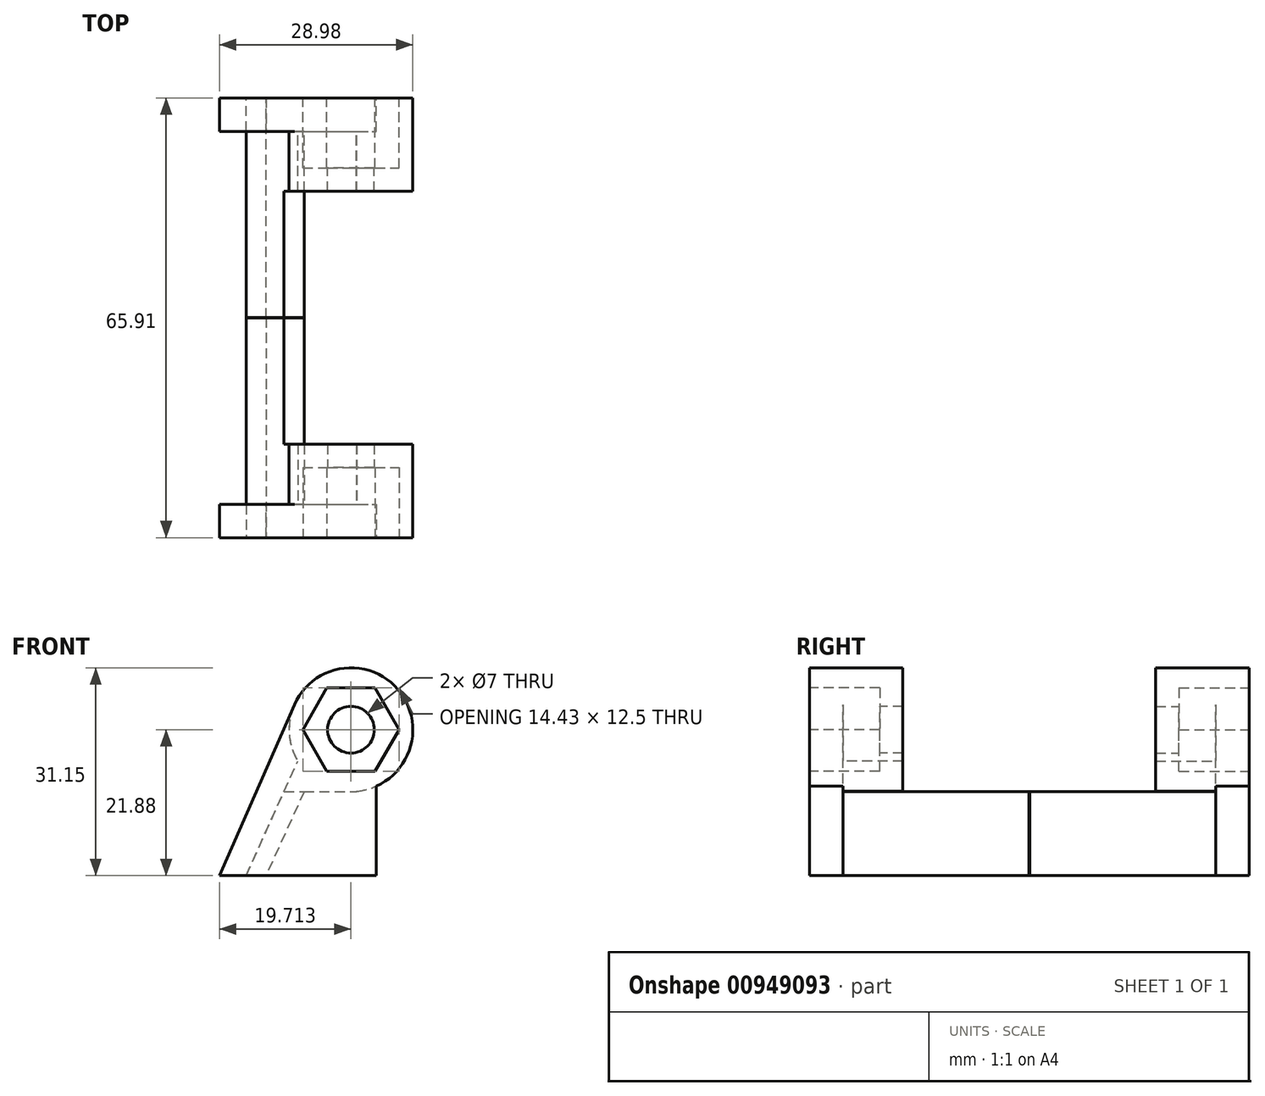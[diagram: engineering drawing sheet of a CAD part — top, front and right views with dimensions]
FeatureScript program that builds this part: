
annotation { "Feature Type Name" : "Feature", "Feature Type Description" : "" }
export const myFeature = defineFeature(function(context is Context, id is Id, definition is map)
    precondition{}
    {
        {
            var Q0;
            Q0=qCreatedBy(makeId("Front.planeOp"),FACE);
            var sketch = newSketch(context, id + "F0", { "sketchPlane" : qUnion([Q0])});
            skLineSegment(sketch, "E0", {"start": v(-38, 25.4) * mm, "end": v(-49, 3.56) * mm});
            skLineSegment(sketch, "E1", {"start": v(-49, 3.56) * mm, "end": v(-25.5, 3.56) * mm});
            skLineSegment(sketch, "E2", {"start": v(-25.5, 3.56) * mm, "end": v(-25.5, 19.16) * mm});
            skLineSegment(sketch, "E3", {"start": v(-25.5, 19.16) * mm, "end": v(-37, 19.16) * mm});
            skLineSegment(sketch, "E4", {"start": v(-37, 19.16) * mm, "end": v(-37, 25.4) * mm});
            skCircle(sketch, "E5", {"center": v(-29.29, 25.4) * mm, "radius": 9.27 * mm});
            skCircle(sketch, "E6.cCircle", {"center": v(-29.29, 25.4) * mm, "radius": 6.25 * mm, "construction": true});
            skLineSegment(sketch, "E6.0", {"start": v(-25.68, 31.66) * mm, "end": v(-22.07, 25.4) * mm});
            skLineSegment(sketch, "E6.1", {"start": v(-22.07, 25.4) * mm, "end": v(-25.68, 19.16) * mm});
            skLineSegment(sketch, "E6.2", {"start": v(-25.68, 19.16) * mm, "end": v(-32.9, 19.16) * mm});
            skLineSegment(sketch, "E6.3", {"start": v(-32.9, 19.16) * mm, "end": v(-36.5, 25.4) * mm});
            skLineSegment(sketch, "E6.4", {"start": v(-36.5, 25.4) * mm, "end": v(-32.9, 31.66) * mm});
            skLineSegment(sketch, "E6.5", {"start": v(-32.9, 31.66) * mm, "end": v(-25.68, 31.66) * mm});
            skCircle(sketch, "E7", {"center": v(-29.29, 25.4) * mm, "radius": 3.5 * mm});
            skPoint(sketch, "E8", {"position": v(-37, 3.56) * mm});
            skLineSegment(sketch, "E9", {"start": v(-37, 19.16) * mm, "end": v(-37, 3.56) * mm});
            skLineSegment(sketch, "E10", {"start": v(-38, 25.4) * mm, "end": v(-37, 25.4) * mm});
            skLineSegment(sketch, "E11", {"start": v(-49, 3.56) * mm, "end": v(-36.67, 31.66) * mm});
            skSolve(sketch);
        }
        {
            var Q0;
            {var subQ0=sQuery(id+"F0.wireOp",EDGE,"E11");var subQ3=sQuery(id+"F0.wireOp",EDGE,"E5");var subQ5=makeQuery(id+"F0.imprint","INTERSECT",VERTEX,{"derivedFrom":[subQ3,subQ0]});Q0=makeQuery(id+"F0.imprint","IMPRINT",FACE,{"disambiguationData":[TD([[makeQuery(id+"F0.imprint","IMPRINT",EDGE,{"disambiguationData":[TD([[subQ5,-1.0]])],"derivedFrom":subQ3}),-1.0]])]});}
            var Q1;
            {var subQ0=sQuery(id+"F0.wireOp",EDGE,"E9");Q1=makeQuery(id+"F0.imprint","IMPRINT",FACE,{"disambiguationData":[TD([[makeQuery(id+"F0.imprint","IMPRINT",EDGE,{"derivedFrom":subQ0}),-1.0]])]});}
            var Q2;
            {var subQ0=sQuery(id+"F0.wireOp",EDGE,"E9");Q2=makeQuery(id+"F0.imprint","IMPRINT",FACE,{"disambiguationData":[TD([[makeQuery(id+"F0.imprint","IMPRINT",EDGE,{"derivedFrom":subQ0}),1.0]])]});}
            var Q3;
            {var subQ1=sQuery(id+"F0.wireOp",EDGE,"E3");var subQ3=sQuery(id+"F0.wireOp",EDGE,"E5");var subQ4=makeQuery(id+"F0.imprint","INTERSECT",VERTEX,{"derivedFrom":[subQ1,subQ3]});Q3=makeQuery(id+"F0.imprint","IMPRINT",FACE,{"disambiguationData":[TD([[makeQuery(id+"F0.imprint","IMPRINT",EDGE,{"disambiguationData":[TD([[subQ4,1.0]])],"derivedFrom":subQ3}),-1.0]])]});}
            extrude(context, id + "F1", {"entities" : qUnion([Q0, Q1, Q2, Q3]), "oppositeDirection" : true, "depth" : 5 * mm, "offsetDistance" : 25.4 * mm});
        }
        {
            var Q0;
            Q0=makeQuery(id+"F0.imprint","IMPRINT",FACE,{"disambiguationData":[TD([[makeQuery(id+"F0.imprint","IMPRINT",EDGE,{"derivedFrom":sQuery(id+"F0.wireOp",EDGE,"E6.0")}),1.0]])]});
            var Q1;
            {var subQ0=sQuery(id+"F0.wireOp",EDGE,"E3");var subQ1=sQuery(id+"F0.wireOp",EDGE,"E2");var subQ2=makeQuery(id+"F0.imprint","INTERSECT",VERTEX,{"derivedFrom":[subQ1,subQ0]});Q1=makeQuery(id+"F0.imprint","IMPRINT",FACE,{"disambiguationData":[TD([[makeQuery(id+"F0.imprint","IMPRINT",EDGE,{"disambiguationData":[TD([[subQ2,1.0]])],"derivedFrom":subQ1}),1.0]])]});}
            var Q2;
            {var subQ0=sQuery(id+"F0.wireOp",EDGE,"E10");Q2=makeQuery(id+"F0.imprint","IMPRINT",FACE,{"disambiguationData":[TD([[makeQuery(id+"F0.imprint","IMPRINT",EDGE,{"derivedFrom":subQ0}),-1.0]])]});}
            var Q3;
            Q3=makeQuery(id+"F0.imprint","IMPRINT",FACE,{"disambiguationData":[TD([[makeQuery(id+"F0.imprint","IMPRINT",EDGE,{"derivedFrom":sQuery(id+"F0.wireOp",EDGE,"E6.0")}),-1.0]])]});
            var Q4;
            Q4 = qSketchRegion(id + "F4", true);
            extrude(context, id + "F2", {"entities" : qUnion([Q0, Q1, Q2, Q3, Q4]), "operationType" : NewBodyOperationType.ADD, "oppositeDirection" : true, "depth" : 14 * mm, "offsetDistance" : 25.4 * mm});
        }
        {
            var Q0;
            Q0=makeQuery(id+"F0.imprint","IMPRINT",FACE,{"disambiguationData":[TD([[makeQuery(id+"F0.imprint","IMPRINT",EDGE,{"derivedFrom":sQuery(id+"F0.wireOp",EDGE,"E6.0")}),-1.0]])]});
            extrude(context, id + "F3", {"entities" : qUnion([Q0]), "operationType" : NewBodyOperationType.REMOVE, "oppositeDirection" : true, "depth" : 10.52 * mm, "offsetDistance" : 25.4 * mm});
        }
        {
            var Q0;
            Q0=qCreatedBy(makeId("Front.planeOp"),FACE);
            var sketch = newSketch(context, id + "F4", { "sketchPlane" : qUnion([Q0])});
            skLineSegment(sketch, "E12", {"start": v(-45, 3.53) * mm, "end": v(-39.32, 16.14) * mm});
            skLineSegment(sketch, "E13", {"start": v(-39.32, 16.14) * mm, "end": v(-36.32, 16.14) * mm});
            skLineSegment(sketch, "E14", {"start": v(-36.32, 16.14) * mm, "end": v(-42, 3.53) * mm});
            skLineSegment(sketch, "E15", {"start": v(-42, 3.53) * mm, "end": v(-45, 3.53) * mm});
            skLineSegment(sketch, "E16", {"start": v(-39.32, 16.14) * mm, "end": v(-28.4, 16.14) * mm});
            skLineSegment(sketch, "E17", {"start": v(-45, 3.53) * mm, "end": v(-36.96, 21.36) * mm});
            skLineSegment(sketch, "E18", {"start": v(-36.96, 21.36) * mm, "end": v(-28.4, 16.14) * mm});
            skSolve(sketch);
        }
        {
            var Q0;
            {var subQ0=sQuery(id+"F4.wireOp",EDGE,"E14");Q0=makeQuery(id+"F4.imprint","IMPRINT",FACE,{"disambiguationData":[TD([[makeQuery(id+"F4.imprint","IMPRINT",EDGE,{"derivedFrom":subQ0}),-1.0]])]});}
            extrude(context, id + "F5", {"entities" : qUnion([Q0]), "operationType" : NewBodyOperationType.ADD, "oppositeDirection" : true, "depth" : 33 * mm, "offsetDistance" : 25.4 * mm});
        }
        {
            var Q0;
            {var subQ4=sQuery(id+"F4.wireOp",EDGE,"E18");Q0=makeQuery(id+"F4.imprint","IMPRINT",FACE,{"disambiguationData":[TD([[makeQuery(id+"F4.imprint","IMPRINT",EDGE,{"derivedFrom":subQ4}),-1.0]])]});}
            extrude(context, id + "F6", {"entities" : qUnion([Q0]), "operationType" : NewBodyOperationType.ADD, "oppositeDirection" : true, "depth" : 14 * mm, "offsetDistance" : 25.4 * mm});
        }
        {
            var Q0;
            Q0=makeQuery(id+"F1.opExtrude","SWEPT_BODY",BODY,{"disambiguationData":[OSD([sQuery(id+"F0.wireOp",EDGE,"E1"),sQuery(id+"F0.wireOp",EDGE,"E2"),sQuery(id+"F0.wireOp",EDGE,"E5"),sQuery(id+"F0.wireOp",EDGE,"E11")])]});
            var Q1;
            Q1=qCreatedBy(makeId("Front.planeOp"),FACE);
            mirror(context, id + "F7", {"entities" : qUnion([Q0]), "mirrorPlane" : qUnion([Q1])});
        }
        {
            var Q0;
            Q0=makeQuery(id+"F1.opExtrude","SWEPT_BODY",BODY,{"disambiguationData":[OSD([sQuery(id+"F0.wireOp",EDGE,"E1"),sQuery(id+"F0.wireOp",EDGE,"E2"),sQuery(id+"F0.wireOp",EDGE,"E5"),sQuery(id+"F0.wireOp",EDGE,"E11")])]});
            var Q1;
            Q1=makeQuery(id+"F2.opExtrude","CAP_EDGE",EDGE,{"disambiguationData":[OSD([sQuery(id+"F0.wireOp",EDGE,"E7")])],"isStart":false});
            var Q2;
            Q2=qCreatedBy(makeId("Front.planeOp"),FACE);
            transform(context, id + "F8", {"entities" : qUnion([Q0]), "transformType" : TransformType.TRANSLATION_DISTANCE, "transformDirection" : qUnion([Q2]), "distance" : 65.9 * mm, "makeCopy" : false});
        }
    });
